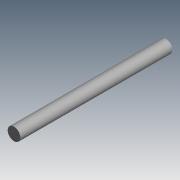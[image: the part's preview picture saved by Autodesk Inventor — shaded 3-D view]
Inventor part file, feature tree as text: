
AUTODESK INVENTOR PART (.ipt)
format: ipt  version: 2015 (Build 190159000, 159)  size: 70,144 bytes
history: native  units: mm
features: extrude x1, sketch x1
ambient origin geometry x8: Origin, YZ Plane, XZ Plane, XY Plane, X Axis, Y Axis, Z Axis, Center Point
bodies: Solid1 (feature_tree)
feature tree (2):
  extrude  "Extrusion1"  Depth=80.0mm TaperAngle=0.0deg
  sketch  "Sketch1"  dims[d0=10.0mm d1=80.0mm d2=0.0mm]
